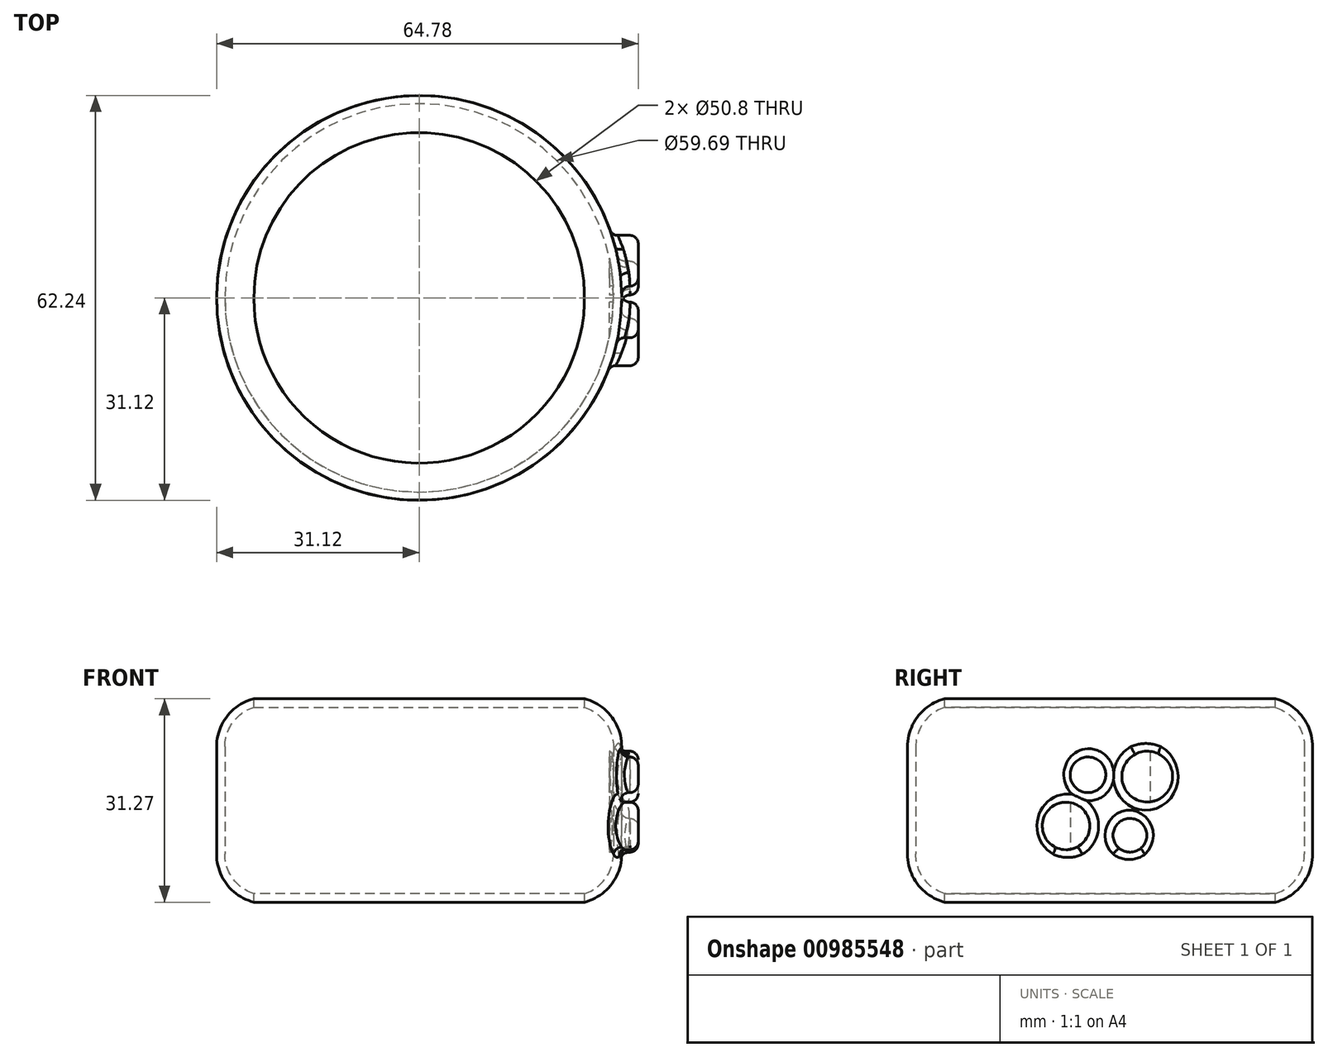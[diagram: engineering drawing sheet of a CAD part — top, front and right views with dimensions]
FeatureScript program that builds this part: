
annotation { "Feature Type Name" : "Feature", "Feature Type Description" : "" }
export const myFeature = defineFeature(function(context is Context, id is Id, definition is map)
    precondition{}
    {
        {
            var Q0;
            Q0=qCreatedBy(makeId("Top.planeOp"),FACE);
            var sketch = newSketch(context, id + "F0", { "sketchPlane" : qUnion([Q0])});
            skCircle(sketch, "E0", {"center": v(0, 0) * mm, "radius": 31.12 * mm});
            skSolve(sketch);
        }
        {
            var Q0;
            Q0 = qSketchRegion(id + "F0", true);
            extrude(context, id + "F1", {"entities" : qUnion([Q0]), "depth" : 31.75 * mm, "offsetDistance" : 25.4 * mm});
        }
        {
            var Q0;
            Q0=makeQuery(id+"F1.opExtrude","CAP_EDGE",EDGE,{"disambiguationData":[OSD([sQuery(id+"F0.wireOp",EDGE,"E0")])],"isStart":false});
            var Q1;
            Q1=makeQuery(id+"F1.opExtrude","SWEPT_FACE",FACE,{"disambiguationData":[OSD([sQuery(id+"F0.wireOp",EDGE,"E0")])]});
            fillet(context, id + "F2", {"entities" : qUnion([Q0, Q1]), "radius" : 7.62 * mm, "tangentPropagation" : true, "allowEdgeOverflow" : false});
        }
        {
            var Q0;
            Q0=makeQuery(id+"F1.opExtrude","CAP_FACE",FACE,{"disambiguationData":[OSD([sQuery(id+"F0.wireOp",EDGE,"E0")])],"isStart":false});
            var sketch = newSketch(context, id + "F3", { "sketchPlane" : qUnion([Q0])});
            skCircle(sketch, "E1", {"center": v(0, 0) * mm, "radius": 25.4 * mm});
            skSolve(sketch);
        }
        {
            var Q0;
            Q0 = qSketchRegion(id + "F3", true);
            extrude(context, id + "F4", {"entities" : qUnion([Q0]), "operationType" : NewBodyOperationType.REMOVE, "oppositeDirection" : true, "depth" : 50.8 * mm, "offsetDistance" : 25.4 * mm});
        }
        {
            var Q0;
            Q0=makeQuery(id+"F4.boolean.opBoolean","COPY",FACE,{"derivedFrom":makeQuery(id+"F4.opExtrude","SWEPT_FACE",FACE,{"disambiguationData":[OSD([sQuery(id+"F3.wireOp",EDGE,"E1")])]})});
            shell(context, id + "F5", {"entities" : qUnion([Q0]), "thickness" : 1.27 * mm});
        }
        {
            var Q0;
            Q0=qCreatedBy(makeId("Right.planeOp"),FACE);
            var sketch = newSketch(context, id + "F6", { "sketchPlane" : qUnion([Q0])});
            skLineSegment(sketch, "E2", {"start": v(0, 0) * mm, "end": v(0, 52.08) * mm});
            skSolve(sketch);
        }
        {
            var Q0;
            Q0=qCreatedBy(makeId("Right.planeOp"),FACE);
            cPlane(context, id + "F7", {"entities" : qUnion([Q0]), "cplaneType" : CPlaneType.OFFSET, "offset" : 29.2 * mm, "width" : 152.4 * mm, "height" : 152.4 * mm});
        }
        {
            var Q0;
            Q0=qCreatedBy(id+"F7.planeOp",FACE);
            var sketch = newSketch(context, id + "F8", { "sketchPlane" : qUnion([Q0])});
            skCircle(sketch, "E3", {"center": v(-6.77, 11.96) * mm, "radius": 3.65 * mm});
            skCircle(sketch, "E4", {"center": v(3.05, 10.52) * mm, "radius": 2.6 * mm});
            skCircle(sketch, "E5", {"center": v(5.7, 19.54) * mm, "radius": 3.9 * mm});
            skCircle(sketch, "E6", {"center": v(-3.4, 19.82) * mm, "radius": 2.74 * mm});
            skSolve(sketch);
        }
        {
            var Q0;
            Q0 = qSketchRegion(id + "F8", true);
            var Q1;
            Q1=sQuery(id+"F8.wireOp",EDGE,"E3");
            var Q2;
            Q2=sQuery(id+"F8.wireOp",EDGE,"E4");
            var Q3;
            Q3=sQuery(id+"F8.wireOp",EDGE,"E5");
            var Q4;
            Q4=sQuery(id+"F8.wireOp",EDGE,"E6");
            extrude(context, id + "F9", {"entities" : qUnion([Q0]), "operationType" : NewBodyOperationType.ADD, "surfaceEntities" : qUnion([Q1, Q2, Q3, Q4]), "depth" : 4.44 * mm, "offsetDistance" : 25.4 * mm});
        }
        {
            var Q0;
            Q0=makeQuery(id+"F9.opExtrude","CAP_EDGE",EDGE,{"disambiguationData":[OSD([sQuery(id+"F8.wireOp",EDGE,"E6")])],"isStart":false});
            var Q1;
            Q1=makeQuery(id+"F9.opExtrude","CAP_EDGE",EDGE,{"disambiguationData":[OSD([sQuery(id+"F8.wireOp",EDGE,"E3")])],"isStart":false});
            var Q2;
            Q2=makeQuery(id+"F9.opExtrude","CAP_EDGE",EDGE,{"disambiguationData":[OSD([sQuery(id+"F8.wireOp",EDGE,"E4")])],"isStart":false});
            var Q3;
            Q3=makeQuery(id+"F9.opExtrude","CAP_EDGE",EDGE,{"disambiguationData":[OSD([sQuery(id+"F8.wireOp",EDGE,"E5")])],"isStart":false});
            fillet(context, id + "F10", {"entities" : qUnion([Q0, Q1, Q2, Q3]), "radius" : 1.27 * mm, "tangentPropagation" : true, "allowEdgeOverflow" : false});
        }
        {
            var Q0;
            Q0=makeQuery(id+"F9.boolean.opBoolean","INTERSECT",EDGE,{"derivedFrom":[makeQuery(id+"F1.opExtrude","SWEPT_FACE",FACE,{"disambiguationData":[OSD([sQuery(id+"F0.wireOp",EDGE,"E0")])]}),makeQuery(id+"F9.opExtrude","SWEPT_FACE",FACE,{"disambiguationData":[OSD([sQuery(id+"F8.wireOp",EDGE,"E6")])]})]});
            var Q1;
            Q1=makeQuery(id+"F9.boolean.opBoolean","INTERSECT",EDGE,{"derivedFrom":[makeQuery(id+"F1.opExtrude","SWEPT_FACE",FACE,{"disambiguationData":[OSD([sQuery(id+"F0.wireOp",EDGE,"E0")])]}),makeQuery(id+"F9.opExtrude","SWEPT_FACE",FACE,{"disambiguationData":[OSD([sQuery(id+"F8.wireOp",EDGE,"E4")])]})]});
            var Q2;
            Q2=makeQuery(id+"F9.boolean.opBoolean","INTERSECT",EDGE,{"derivedFrom":[makeQuery(id+"F1.opExtrude","SWEPT_FACE",FACE,{"disambiguationData":[OSD([sQuery(id+"F0.wireOp",EDGE,"E0")])]}),makeQuery(id+"F9.opExtrude","SWEPT_FACE",FACE,{"disambiguationData":[OSD([sQuery(id+"F8.wireOp",EDGE,"E3")])]})]});
            var Q3;
            Q3=makeQuery(id+"F9.boolean.opBoolean","INTERSECT",EDGE,{"derivedFrom":[makeQuery(id+"F1.opExtrude","SWEPT_FACE",FACE,{"disambiguationData":[OSD([sQuery(id+"F0.wireOp",EDGE,"E0")])]}),makeQuery(id+"F9.opExtrude","SWEPT_FACE",FACE,{"disambiguationData":[OSD([sQuery(id+"F8.wireOp",EDGE,"E5")])]})]});
            fillet(context, id + "F11", {"entities" : qUnion([Q0, Q1, Q2, Q3]), "radius" : 1.27 * mm, "tangentPropagation" : true, "allowEdgeOverflow" : false});
        }
    });
